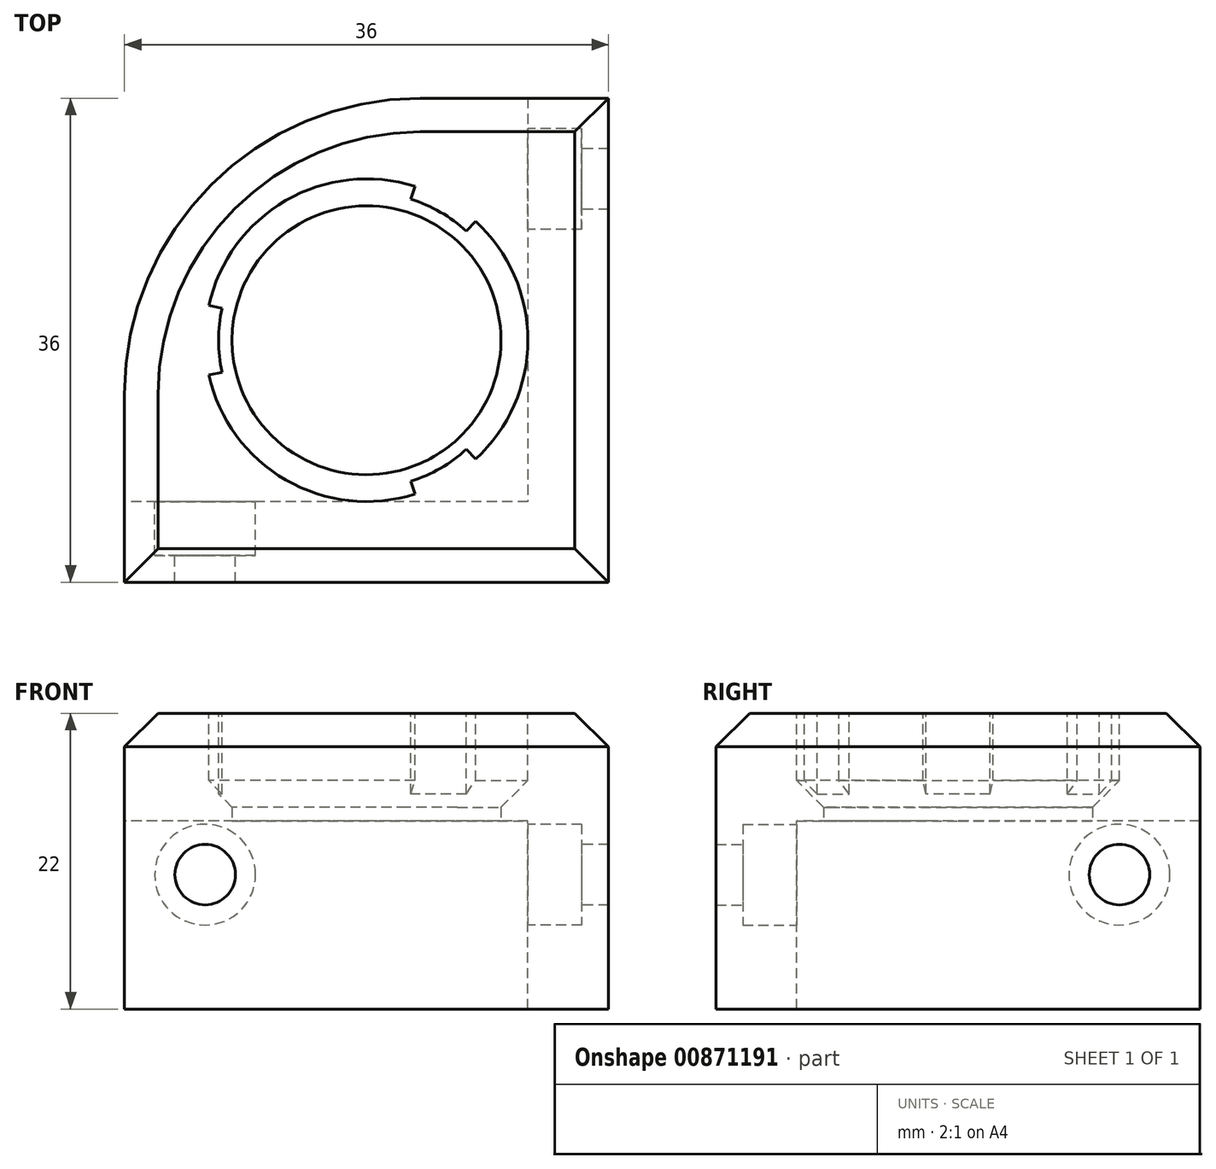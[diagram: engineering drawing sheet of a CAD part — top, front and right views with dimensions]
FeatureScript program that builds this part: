
annotation { "Feature Type Name" : "Feature", "Feature Type Description" : "" }
export const myFeature = defineFeature(function(context is Context, id is Id, definition is map)
    precondition{}
    {
        {
            var Q0;
            Q0=qCreatedBy(makeId("Top.planeOp"),FACE);
            var sketch = newSketch(context, id + "F0", { "sketchPlane" : qUnion([Q0])});
            skLineSegment(sketch, "E0.bottom", {"start": v(0, 0) * mm, "end": v(36, 0) * mm});
            skLineSegment(sketch, "E0.top", {"start": v(0, 36) * mm, "end": v(36, 36) * mm});
            skLineSegment(sketch, "E0.left", {"start": v(0, 0) * mm, "end": v(0, 36) * mm});
            skLineSegment(sketch, "E0.right", {"start": v(36, 0) * mm, "end": v(36, 36) * mm});
            skCircle(sketch, "E1", {"center": v(18, 18) * mm, "radius": 10 * mm});
            skPoint(sketch, "E1.centerSnap0", {"position": v(36, 18) * mm});
            skPoint(sketch, "E1.centerSnap1", {"position": v(18, 36) * mm});
            skSolve(sketch);
        }
        {
            var Q0;
            Q0 = qSketchRegion(id + "F0", true);
            extrude(context, id + "F1", {"entities" : qUnion([Q0]), "depth" : 8 * mm, "offsetDistance" : 25 * mm});
        }
        {
            var Q0;
            Q0=makeQuery(id+"F1.opExtrude","CAP_FACE",FACE,{"disambiguationData":[OSD([sQuery(id+"F0.wireOp",EDGE,"E0.bottom"),sQuery(id+"F0.wireOp",EDGE,"E0.top"),sQuery(id+"F0.wireOp",EDGE,"E0.left"),sQuery(id+"F0.wireOp",EDGE,"E0.right"),sQuery(id+"F0.wireOp",EDGE,"E1")])],"isStart":true});
            var sketch = newSketch(context, id + "F2", { "sketchPlane" : qUnion([Q0])});
            skLineSegment(sketch, "E2", {"start": v(0, 0) * mm, "end": v(36, 0) * mm});
            skLineSegment(sketch, "E3", {"start": v(36, 0) * mm, "end": v(36, -36) * mm});
            skLineSegment(sketch, "E4", {"start": v(36, -36) * mm, "end": v(30, -36) * mm});
            skLineSegment(sketch, "E5", {"start": v(30, -36) * mm, "end": v(30, -6) * mm});
            skLineSegment(sketch, "E6", {"start": v(30, -6) * mm, "end": v(0, -6) * mm});
            skLineSegment(sketch, "E7", {"start": v(0, -6) * mm, "end": v(0, 0) * mm});
            skSolve(sketch);
        }
        {
            var Q0;
            Q0=makeQuery(id+"F2.imprint","IMPRINT",FACE,{"disambiguationData":[TD([[makeQuery(id+"F2.imprint","IMPRINT",EDGE,{"derivedFrom":sQuery(id+"F2.wireOp",EDGE,"E2")}),-1.0]])]});
            extrude(context, id + "F3", {"entities" : qUnion([Q0]), "operationType" : NewBodyOperationType.ADD, "depth" : 14 * mm, "offsetDistance" : 25 * mm});
        }
        {
            var Q0;
            Q0=makeQuery(id+"F3.opExtrude","SWEPT_FACE",FACE,{"disambiguationData":[OSD([sQuery(id+"F2.wireOp",EDGE,"E6")])]});
            var sketch = newSketch(context, id + "F4", { "sketchPlane" : qUnion([Q0])});
            skCircle(sketch, "E8", {"center": v(-6, -4) * mm, "radius": 2.25 * mm});
            skSolve(sketch);
        }
        {
            var Q0;
            Q0 = qSketchRegion(id + "F4", true);
            extrude(context, id + "F5", {"entities" : qUnion([Q0]), "operationType" : NewBodyOperationType.REMOVE, "endBound" : BoundingType.THROUGH_ALL, "oppositeDirection" : true, "depth" : 25 * mm, "offsetDistance" : 25 * mm});
        }
        {
            var Q0;
            Q0=makeQuery(id+"F3.opExtrude","SWEPT_FACE",FACE,{"disambiguationData":[OSD([sQuery(id+"F2.wireOp",EDGE,"E6")])]});
            var sketch = newSketch(context, id + "F6", { "sketchPlane" : qUnion([Q0])});
            skCircle(sketch, "E9", {"center": v(-6, -4) * mm, "radius": 3.75 * mm});
            skSolve(sketch);
        }
        {
            var Q0;
            Q0 = qSketchRegion(id + "F6", true);
            extrude(context, id + "F7", {"entities" : qUnion([Q0]), "operationType" : NewBodyOperationType.REMOVE, "oppositeDirection" : true, "depth" : 4 * mm, "offsetDistance" : 25 * mm});
        }
        {
            var Q0;
            Q0=makeQuery(id+"F3.opExtrude","SWEPT_FACE",FACE,{"disambiguationData":[OSD([sQuery(id+"F2.wireOp",EDGE,"E5")])]});
            var sketch = newSketch(context, id + "F8", { "sketchPlane" : qUnion([Q0])});
            skCircle(sketch, "E10", {"center": v(-30, -4) * mm, "radius": 2.25 * mm});
            skSolve(sketch);
        }
        {
            var Q0;
            Q0 = qSketchRegion(id + "F8", true);
            extrude(context, id + "F9", {"entities" : qUnion([Q0]), "operationType" : NewBodyOperationType.REMOVE, "endBound" : BoundingType.THROUGH_ALL, "oppositeDirection" : true, "depth" : 25 * mm, "offsetDistance" : 25 * mm});
        }
        {
            var Q0;
            Q0=makeQuery(id+"F3.opExtrude","SWEPT_FACE",FACE,{"disambiguationData":[OSD([sQuery(id+"F2.wireOp",EDGE,"E5")])]});
            var sketch = newSketch(context, id + "F10", { "sketchPlane" : qUnion([Q0])});
            skCircle(sketch, "E11", {"center": v(-30, -4) * mm, "radius": 3.75 * mm});
            skSolve(sketch);
        }
        {
            var Q0;
            Q0 = qSketchRegion(id + "F10", true);
            extrude(context, id + "F11", {"entities" : qUnion([Q0]), "operationType" : NewBodyOperationType.REMOVE, "oppositeDirection" : true, "depth" : 4 * mm, "offsetDistance" : 25 * mm});
        }
        {
            var Q0;
            Q0=makeQuery(id+"F1.opExtrude","CAP_FACE",FACE,{"disambiguationData":[OSD([sQuery(id+"F0.wireOp",EDGE,"E0.bottom"),sQuery(id+"F0.wireOp",EDGE,"E0.top"),sQuery(id+"F0.wireOp",EDGE,"E0.left"),sQuery(id+"F0.wireOp",EDGE,"E0.right"),sQuery(id+"F0.wireOp",EDGE,"E1")])],"isStart":false});
            var sketch = newSketch(context, id + "F12", { "sketchPlane" : qUnion([Q0])});
            skArc(sketch, "E12", {"start": v(21.6, 29.44) * mm, "mid": v(12, 28.4) * mm, "end": v(6.28, 20.6) * mm});
            skArc(sketch, "E13", {"start": v(7.26, 20.38) * mm, "mid": v(7, 18) * mm, "end": v(7.26, 15.62) * mm});
            skLineSegment(sketch, "E14", {"start": v(7.26, 20.38) * mm, "end": v(6.28, 20.6) * mm});
            skLineSegment(sketch, "E15", {"start": v(7.26, 15.62) * mm, "end": v(6.28, 15.4) * mm});
            skLineSegment(sketch, "E16.1.0", {"start": v(25.43, 9.89) * mm, "end": v(26.1, 9.15) * mm});
            skLineSegment(sketch, "E16.1.1", {"start": v(21.3, 7.5) * mm, "end": v(21.6, 6.56) * mm});
            skLineSegment(sketch, "E16.2.0", {"start": v(21.3, 28.5) * mm, "end": v(21.6, 29.44) * mm});
            skLineSegment(sketch, "E16.2.1", {"start": v(25.43, 26.11) * mm, "end": v(26.1, 26.85) * mm});
            skArc(sketch, "E17.trimOffspring", {"start": v(21.3, 7.5) * mm, "mid": v(23.5, 8.47) * mm, "end": v(25.43, 9.89) * mm});
            skArc(sketch, "E18.trimOffspring", {"start": v(25.43, 26.11) * mm, "mid": v(23.5, 27.53) * mm, "end": v(21.3, 28.5) * mm});
            skArc(sketch, "E19.trimOffspring", {"start": v(26.1, 9.15) * mm, "mid": v(30, 18) * mm, "end": v(26.1, 26.85) * mm});
            skArc(sketch, "E20.trimOffspring", {"start": v(6.28, 15.4) * mm, "mid": v(12, 7.6) * mm, "end": v(21.6, 6.56) * mm});
            skSolve(sketch);
        }
        {
            var Q0;
            Q0 = qSketchRegion(id + "F12", true);
            extrude(context, id + "F13", {"entities" : qUnion([Q0]), "operationType" : NewBodyOperationType.REMOVE, "oppositeDirection" : true, "depth" : 7 * mm, "offsetDistance" : 25 * mm});
        }
        {
            var Q0;
            Q0=makeQuery(id+"F1.opExtrude","SWEPT_EDGE",EDGE,{"disambiguationData":[OSD([sQuery(id+"F0.wireOp",EDGE,"E0.top"),sQuery(id+"F0.wireOp",EDGE,"E0.left")])]});
            fillet(context, id + "F14", {"entities" : qUnion([Q0]), "radius" : 22 * mm, "tangentPropagation" : true, "allowEdgeOverflow" : false});
        }
        {
            var Q0;
            Q0=makeQuery(id+"F1.opExtrude","CAP_EDGE",EDGE,{"disambiguationData":[OSD([sQuery(id+"F0.wireOp",EDGE,"E0.right")])],"isStart":false});
            var Q1;
            Q1=makeQuery(id+"F1.opExtrude","CAP_EDGE",EDGE,{"disambiguationData":[OSD([sQuery(id+"F0.wireOp",EDGE,"E0.bottom")])],"isStart":false});
            var Q2;
            Q2=makeQuery(id+"F1.opExtrude","CAP_EDGE",EDGE,{"disambiguationData":[OSD([sQuery(id+"F0.wireOp",EDGE,"E0.top")])],"isStart":false});
            var Q3;
            Q3=makeQuery(id+"F1.opExtrude","CAP_EDGE",EDGE,{"disambiguationData":[OSD([sQuery(id+"F0.wireOp",EDGE,"E0.left")])],"isStart":false});
            chamfer(context, id + "F15", {"entities" : qUnion([Q0, Q1, Q2, Q3]), "width" : 2.5 * mm, "tangentPropagation" : true});
        }
        {
            var Q0;
            Q0=makeQuery(id+"F13.boolean.opBoolean","COPY",EDGE,{"derivedFrom":makeQuery(id+"F13.opExtrude","CAP_EDGE",EDGE,{"disambiguationData":[OSD([sQuery(id+"F12.wireOp",EDGE,"E17.trimOffspring")])],"isStart":false})});
            var Q1;
            Q1=makeQuery(id+"F13.boolean.opBoolean","COPY",EDGE,{"derivedFrom":makeQuery(id+"F13.opExtrude","CAP_EDGE",EDGE,{"disambiguationData":[OSD([sQuery(id+"F12.wireOp",EDGE,"E13")])],"isStart":false})});
            var Q2;
            Q2=makeQuery(id+"F13.boolean.opBoolean","COPY",EDGE,{"derivedFrom":makeQuery(id+"F13.opExtrude","CAP_EDGE",EDGE,{"disambiguationData":[OSD([sQuery(id+"F12.wireOp",EDGE,"E18.trimOffspring")])],"isStart":false})});
            var Q3;
            Q3=makeQuery(id+"F13.boolean.opBoolean","COPY",EDGE,{"derivedFrom":makeQuery(id+"F13.opExtrude","CAP_EDGE",EDGE,{"disambiguationData":[OSD([sQuery(id+"F12.wireOp",EDGE,"E13")])],"isStart":true})});
            var Q4;
            Q4=makeQuery(id+"F13.boolean.opBoolean","COPY",EDGE,{"derivedFrom":makeQuery(id+"F13.opExtrude","CAP_EDGE",EDGE,{"disambiguationData":[OSD([sQuery(id+"F12.wireOp",EDGE,"E18.trimOffspring")])],"isStart":true})});
            var Q5;
            Q5=makeQuery(id+"F13.boolean.opBoolean","COPY",EDGE,{"derivedFrom":makeQuery(id+"F13.opExtrude","CAP_EDGE",EDGE,{"disambiguationData":[OSD([sQuery(id+"F12.wireOp",EDGE,"E17.trimOffspring")])],"isStart":true})});
            chamfer(context, id + "F16", {"entities" : qUnion([Q0, Q1, Q2, Q3, Q4, Q5]), "width" : 1 * mm, "tangentPropagation" : true});
        }
        {
            var Q0;
            Q0=makeQuery(id+"F13.boolean.opBoolean","COPY",EDGE,{"derivedFrom":makeQuery(id+"F13.opExtrude","CAP_EDGE",EDGE,{"disambiguationData":[OSD([sQuery(id+"F12.wireOp",EDGE,"E19.trimOffspring")])],"isStart":false})});
            var Q1;
            Q1=makeQuery(id+"F13.boolean.opBoolean","COPY",EDGE,{"derivedFrom":makeQuery(id+"F13.opExtrude","CAP_EDGE",EDGE,{"disambiguationData":[OSD([sQuery(id+"F12.wireOp",EDGE,"E20.trimOffspring")])],"isStart":false})});
            var Q2;
            Q2=makeQuery(id+"F13.boolean.opBoolean","COPY",EDGE,{"derivedFrom":makeQuery(id+"F13.opExtrude","CAP_EDGE",EDGE,{"disambiguationData":[OSD([sQuery(id+"F12.wireOp",EDGE,"E12")])],"isStart":false})});
            chamfer(context, id + "F17", {"entities" : qUnion([Q0, Q1, Q2]), "width" : 2 * mm, "tangentPropagation" : true});
        }
    });
